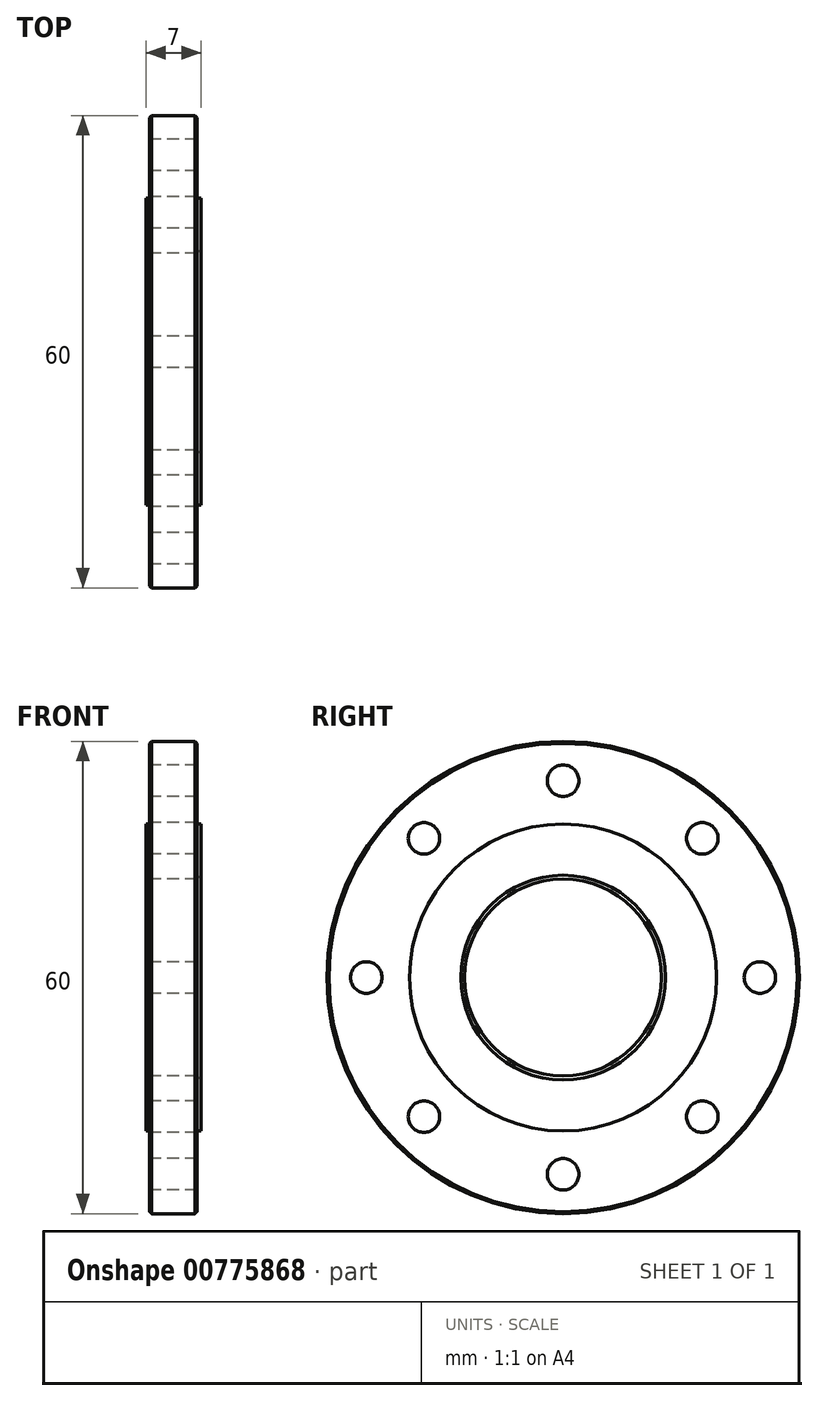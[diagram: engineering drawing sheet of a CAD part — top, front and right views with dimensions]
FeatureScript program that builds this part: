
annotation { "Feature Type Name" : "Feature", "Feature Type Description" : "" }
export const myFeature = defineFeature(function(context is Context, id is Id, definition is map)
    precondition{}
    {
        {
            var Q0;
            Q0=qCreatedBy(makeId("Right.planeOp"),FACE);
            var sketch = newSketch(context, id + "F0", { "sketchPlane" : qUnion([Q0])});
            skCircle(sketch, "E0", {"center": v(0, 0) * mm, "radius": 30 * mm});
            skCircle(sketch, "E1", {"center": v(0, 0) * mm, "radius": 19.5 * mm});
            skCircle(sketch, "E2", {"center": v(0, 0) * mm, "radius": 12.5 * mm});
            skCircle(sketch, "E3", {"center": v(0, 25) * mm, "radius": 2 * mm});
            skCircle(sketch, "E4.1.0", {"center": v(17.68, 17.68) * mm, "radius": 2 * mm});
            skCircle(sketch, "E4.2.0", {"center": v(25, 0) * mm, "radius": 2 * mm});
            skLineSegment(sketch, "E4.anchor1", {"start": v(0, 0) * mm, "end": v(0, 25) * mm, "construction": true});
            skLineSegment(sketch, "E4.anchor2", {"start": v(0, 0) * mm, "end": v(-17.68, 17.68) * mm, "construction": true});
            skCircle(sketch, "E5.1.3.0", {"center": v(17.68, -17.68) * mm, "radius": 2 * mm});
            skCircle(sketch, "E5.1.4.0", {"center": v(0, -25) * mm, "radius": 2 * mm});
            skCircle(sketch, "E5.1.5.0", {"center": v(-17.68, -17.68) * mm, "radius": 2 * mm});
            skCircle(sketch, "E5.1.6.0", {"center": v(-25, 0) * mm, "radius": 2 * mm});
            skCircle(sketch, "E5.1.7.0", {"center": v(-17.68, 17.68) * mm, "radius": 2 * mm});
            skSolve(sketch);
        }
        {
            var Q0;
            Q0=makeQuery(id+"F0.imprint","IMPRINT",FACE,{"disambiguationData":[TD([[makeQuery(id+"F0.imprint","IMPRINT",EDGE,{"derivedFrom":sQuery(id+"F0.wireOp",EDGE,"E0")}),1.0]])]});
            extrude(context, id + "F1", {"entities" : qUnion([Q0]), "endBound" : BoundingType.SYMMETRIC, "depth" : 6 * mm, "offsetDistance" : 25.4 * mm});
        }
        {
            var Q0;
            Q0=makeQuery(id+"F0.imprint","IMPRINT",FACE,{"disambiguationData":[TD([[makeQuery(id+"F0.imprint","IMPRINT",EDGE,{"derivedFrom":sQuery(id+"F0.wireOp",EDGE,"E1")}),1.0]])]});
            extrude(context, id + "F2", {"entities" : qUnion([Q0]), "operationType" : NewBodyOperationType.ADD, "endBound" : BoundingType.SYMMETRIC, "depth" : 7 * mm, "offsetDistance" : 25.4 * mm});
        }
        {
            var Q0;
            Q0=makeQuery(id+"F2.opExtrude","SWEPT_FACE",FACE,{"disambiguationData":[OSD([sQuery(id+"F0.wireOp",EDGE,"E2")])]});
            chamfer(context, id + "F3", {"entities" : qUnion([Q0]), "width" : .5 * mm, "tangentPropagation" : true});
        }
        {
            var Q0;
            Q0=makeQuery(id+"F1.opExtrude","SWEPT_FACE",FACE,{"disambiguationData":[OSD([sQuery(id+"F0.wireOp",EDGE,"E0")])]});
            chamfer(context, id + "F4", {"entities" : qUnion([Q0]), "width" : .25 * mm, "tangentPropagation" : true});
        }
    });
